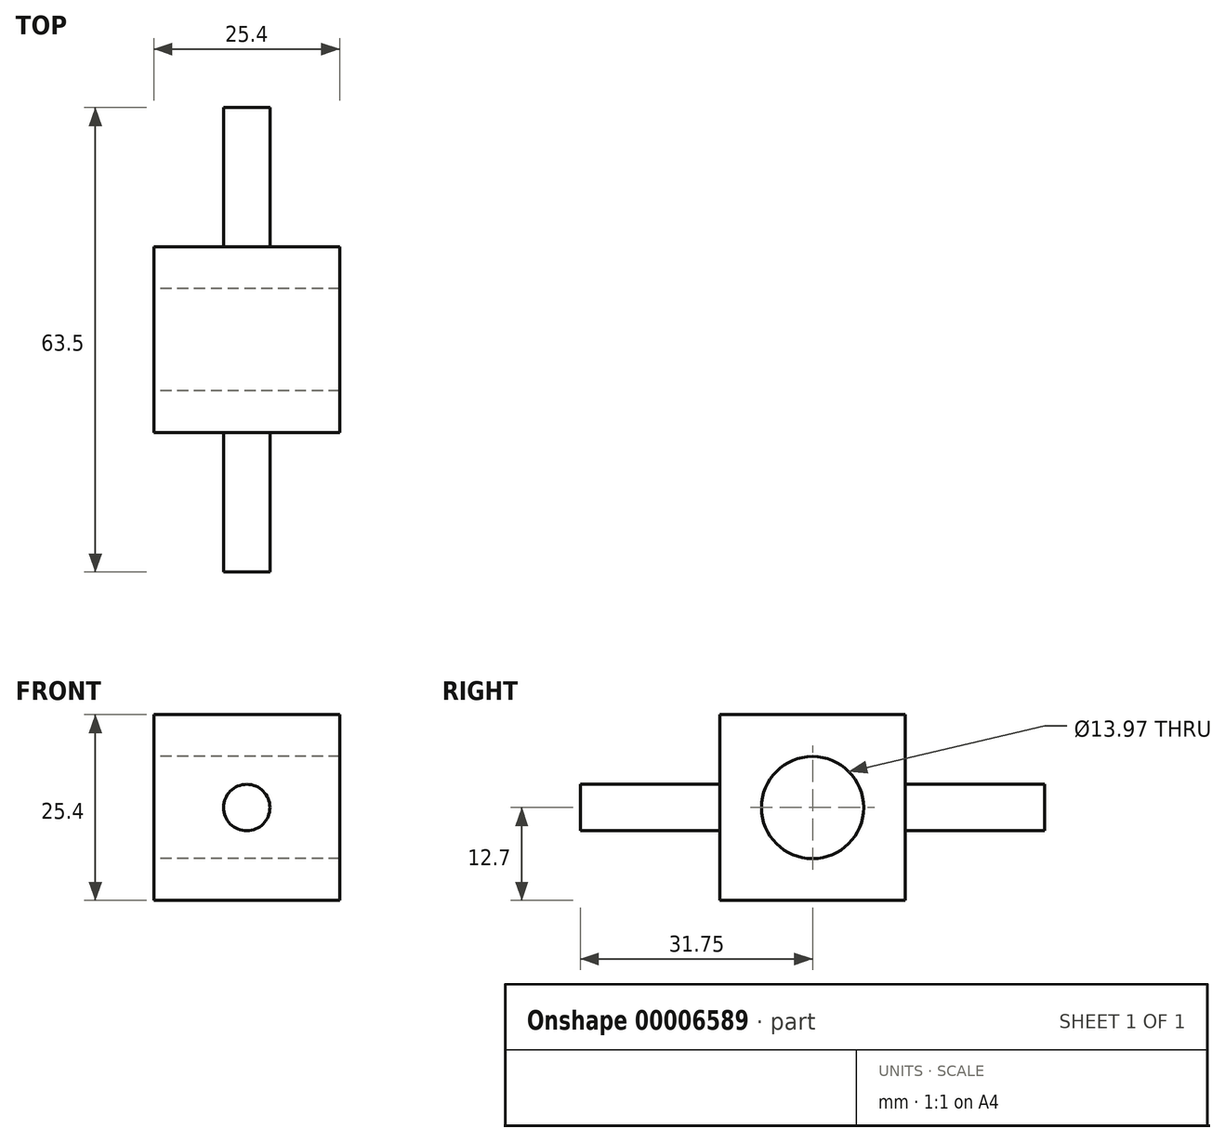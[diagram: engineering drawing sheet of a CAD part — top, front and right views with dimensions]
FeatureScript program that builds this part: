
annotation { "Feature Type Name" : "Feature", "Feature Type Description" : "" }
export const myFeature = defineFeature(function(context is Context, id is Id, definition is map)
    precondition{}
    {
        {
            var Q0;
            Q0=qCreatedBy(makeId("Front.planeOp"),FACE);
            var sketch = newSketch(context, id + "F0", { "sketchPlane" : qUnion([Q0])});
            skLineSegment(sketch, "E0.bottom", {"start": v(-12.7, 12.7) * mm, "end": v(12.7, 12.7) * mm});
            skLineSegment(sketch, "E0.top", {"start": v(-12.7, -12.7) * mm, "end": v(12.7, -12.7) * mm});
            skLineSegment(sketch, "E0.left", {"start": v(-12.7, 12.7) * mm, "end": v(-12.7, -12.7) * mm});
            skLineSegment(sketch, "E0.right", {"start": v(12.7, 12.7) * mm, "end": v(12.7, -12.7) * mm});
            skSolve(sketch);
        }
        {
            var Q0;
            Q0 = qSketchRegion(id + "F0", true);
            extrude(context, id + "F1", {"entities" : qUnion([Q0]), "depth" : 25.4 * mm});
        }
        {
            var Q0;
            Q0=makeQuery(id+"F1.opExtrude","CAP_FACE",FACE,{"disambiguationData":[OSD([sQuery(id+"F0.wireOp",EDGE,"E0.bottom"),sQuery(id+"F0.wireOp",EDGE,"E0.top"),sQuery(id+"F0.wireOp",EDGE,"E0.left"),sQuery(id+"F0.wireOp",EDGE,"E0.right")])],"isStart":false});
            var sketch = newSketch(context, id + "F2", { "sketchPlane" : qUnion([Q0])});
            skCircle(sketch, "E1", {"center": v(0, 0) * mm, "radius": 3.18 * mm});
            skSolve(sketch);
        }
        {
            var Q0;
            Q0 = qSketchRegion(id + "F2", true);
            extrude(context, id + "F3", {"entities" : qUnion([Q0]), "operationType" : NewBodyOperationType.ADD, "depth" : 19.05 * mm});
        }
        {
            var Q0;
            Q0 = qSketchRegion(id + "F2", true);
            extrude(context, id + "F4", {"entities" : qUnion([Q0]), "operationType" : NewBodyOperationType.ADD, "oppositeDirection" : true, "depth" : 44.45 * mm});
        }
        {
            var Q0;
            Q0=makeQuery(id+"F1.opExtrude","SWEPT_FACE",FACE,{"disambiguationData":[OSD([sQuery(id+"F0.wireOp",EDGE,"E0.left")])]});
            var sketch = newSketch(context, id + "F5", { "sketchPlane" : qUnion([Q0])});
            skCircle(sketch, "E2", {"center": v(12.7, 0) * mm, "radius": 6.99 * mm});
            skSolve(sketch);
        }
        {
            var Q0;
            Q0 = qSketchRegion(id + "F5", true);
            extrude(context, id + "F6", {"entities" : qUnion([Q0]), "operationType" : NewBodyOperationType.REMOVE, "oppositeDirection" : true, "depth" : 50.8 * mm});
        }
    });
